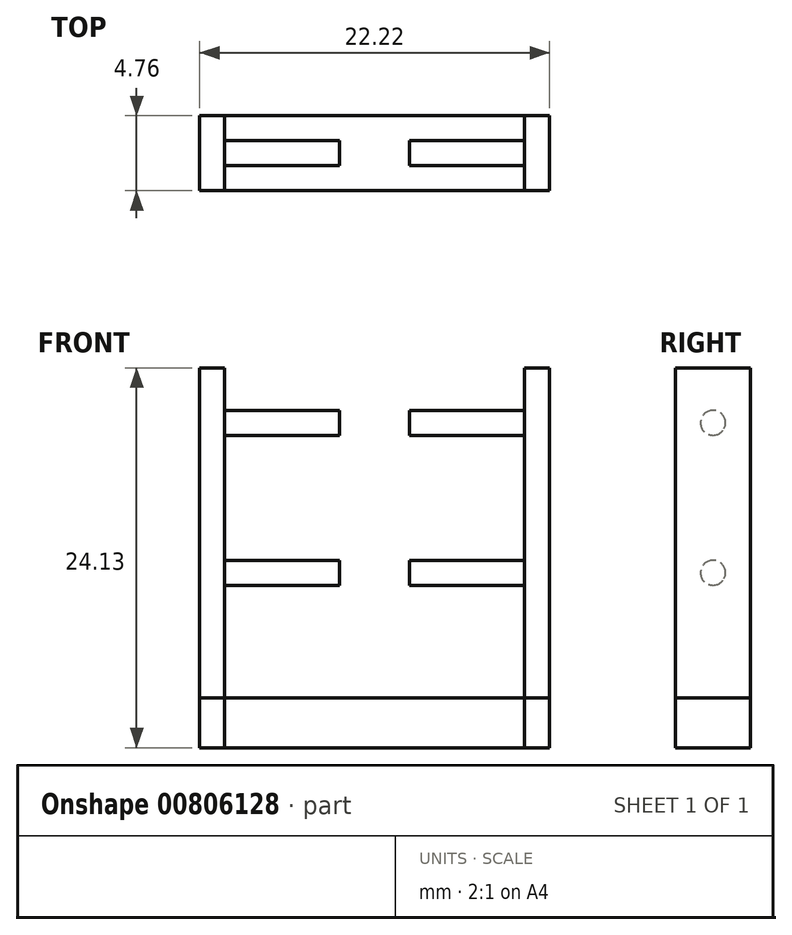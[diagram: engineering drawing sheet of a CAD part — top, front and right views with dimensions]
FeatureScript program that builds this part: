
annotation { "Feature Type Name" : "Feature", "Feature Type Description" : "" }
export const myFeature = defineFeature(function(context is Context, id is Id, definition is map)
    precondition{}
    {
        {
            var Q0;
            Q0=qCreatedBy(makeId("Top.planeOp"),FACE);
            var sketch = newSketch(context, id + "F0", { "sketchPlane" : qUnion([Q0])});
            skLineSegment(sketch, "E0.bottom", {"start": v(-11.11, 2.38) * mm, "end": v(11.11, 2.38) * mm});
            skLineSegment(sketch, "E0.top", {"start": v(-11.11, -2.38) * mm, "end": v(11.11, -2.38) * mm});
            skLineSegment(sketch, "E0.left", {"start": v(-11.11, 2.38) * mm, "end": v(-11.11, -2.38) * mm});
            skLineSegment(sketch, "E0.right", {"start": v(11.11, 2.38) * mm, "end": v(11.11, -2.38) * mm});
            skPoint(sketch, "E0.middle", {"position": v(0, 0) * mm});
            skLineSegment(sketch, "E1", {"start": v(-9.53, 2.38) * mm, "end": v(-9.53, -2.38) * mm});
            skLineSegment(sketch, "E2", {"start": v(9.53, 2.38) * mm, "end": v(9.53, -2.38) * mm});
            skSolve(sketch);
        }
        {
            var Q0;
            {var subQ0=sQuery(id+"F0.wireOp",EDGE,"E0.left");Q0=makeQuery(id+"F0.imprint","IMPRINT",FACE,{"disambiguationData":[TD([[makeQuery(id+"F0.imprint","IMPRINT",EDGE,{"derivedFrom":subQ0}),1.0]])]});}
            var Q1;
            {var subQ0=sQuery(id+"F0.wireOp",EDGE,"E0.right");Q1=makeQuery(id+"F0.imprint","IMPRINT",FACE,{"disambiguationData":[TD([[makeQuery(id+"F0.imprint","IMPRINT",EDGE,{"derivedFrom":subQ0}),-1.0]])]});}
            extrude(context, id + "F1", {"entities" : qUnion([Q0, Q1]), "depth" : 24.13 * mm, "offsetDistance" : 25.4 * mm});
        }
        {
            var Q0;
            Q0 = qSketchRegion(id + "F0", true);
            extrude(context, id + "F2", {"entities" : qUnion([Q0]), "depth" : 3.17 * mm, "offsetDistance" : 25.4 * mm});
        }
        {
            var Q0;
            Q0=makeQuery(id+"F1.opExtrude","SWEPT_FACE",FACE,{"disambiguationData":[OSD([sQuery(id+"F0.wireOp",EDGE,"E0.right")])]});
            var sketch = newSketch(context, id + "F3", { "sketchPlane" : qUnion([Q0])});
            skLineSegment(sketch, "E3", {"start": v(0, 24.13) * mm, "end": v(0, 0) * mm, "construction": true});
            skCircle(sketch, "E4", {"center": v(0, 11.11) * mm, "radius": 0.8 * mm});
            skCircle(sketch, "E5", {"center": v(0, 20.64) * mm, "radius": 0.8 * mm});
            skSolve(sketch);
        }
        {
            var Q0;
            Q0 = qSketchRegion(id + "F3", true);
            extrude(context, id + "F4", {"entities" : qUnion([Q0]), "operationType" : NewBodyOperationType.ADD, "oppositeDirection" : true, "depth" : 8.9 * mm, "offsetDistance" : 25.4 * mm});
        }
        {
            var Q0;
            Q0=makeQuery(id+"F1.opExtrude","SWEPT_FACE",FACE,{"disambiguationData":[OSD([sQuery(id+"F0.wireOp",EDGE,"E0.left")])]});
            var sketch = newSketch(context, id + "F5", { "sketchPlane" : qUnion([Q0])});
            skLineSegment(sketch, "E6", {"start": v(0, 24.13) * mm, "end": v(0, 0) * mm, "construction": true});
            skCircle(sketch, "E7", {"center": v(0, 11.11) * mm, "radius": 0.8 * mm});
            skCircle(sketch, "E8", {"center": v(0, 20.64) * mm, "radius": 0.8 * mm});
            skSolve(sketch);
        }
        {
            var Q0;
            Q0 = qSketchRegion(id + "F5", true);
            extrude(context, id + "F6", {"entities" : qUnion([Q0]), "operationType" : NewBodyOperationType.ADD, "oppositeDirection" : true, "depth" : 8.9 * mm, "offsetDistance" : 25.4 * mm});
        }
    });
